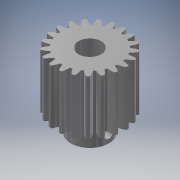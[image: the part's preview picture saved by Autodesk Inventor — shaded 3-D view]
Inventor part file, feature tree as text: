
AUTODESK INVENTOR PART (.ipt)
format: ipt  version: 2017 (Build 210142000, 142)  size: 268,800 bytes
history: native  units: mm (DEFAULTED — no unit token found)
features: plane x5, sketch x5, extrude x4, other x3, fillet x1
ambient origin geometry x8: Origin, YZ Plane, XZ Plane, XY Plane, X Axis, Y Axis, Z Axis, Center Point
bodies: Solid1 (feature_tree)
feature tree (18):
  extrude  "Extrusion1"  Depth=20.0mm TaperAngle=0.0deg
  plane  "Work Plane2"
  plane  "Work Plane8"
  plane  "Work Plane9"
  other  "Spur Gear"
  plane  "Work Plane12"
  extrude  "Extrusion3"  Depth=10.0mm TaperAngle=0.0deg
  extrude  "Extrusion4"  Depth=1.495997mm TaperAngle=0.0deg
  fillet  "Fillet1"  [1 undecoded]
  plane  "Work Plane13"
  extrude  "Extrusion5"  Depth=42.0mm
  sketch  "Sketch1"  dims[d0=25.850265mm d1=20.0mm d2=0.0mm]
  sketch  "Sketch2"  dims[d3=23.837838mm d4=10.0mm d5=0.0mm]
  other  "Srf1"
  sketch  "Sketch4"  dims[d16=42.0mm d17=0.0mm d34=1.495997mm d39=0.0mm]
  sketch  "Sketch5"  dims[d41=0.0mm d43=42.0mm]
  sketch  "Sketch7"  dims[d46=42.0mm d47=0.0mm d48=0.0mm d55=26.0mm d56=0.0mm d57=8.35mm d58=14.0mm d59=7.0mm d60=0.0mm d61=1.0mm d63=3.4mm d64=20.0mm d65=0.0mm]
  other  "Pitch Diameter"
note: 1 required parameter value undecoded (feature->parameter linkage not recoverable at this tier; creation-order binding heuristic only, values carry confidence <= 0.55)
